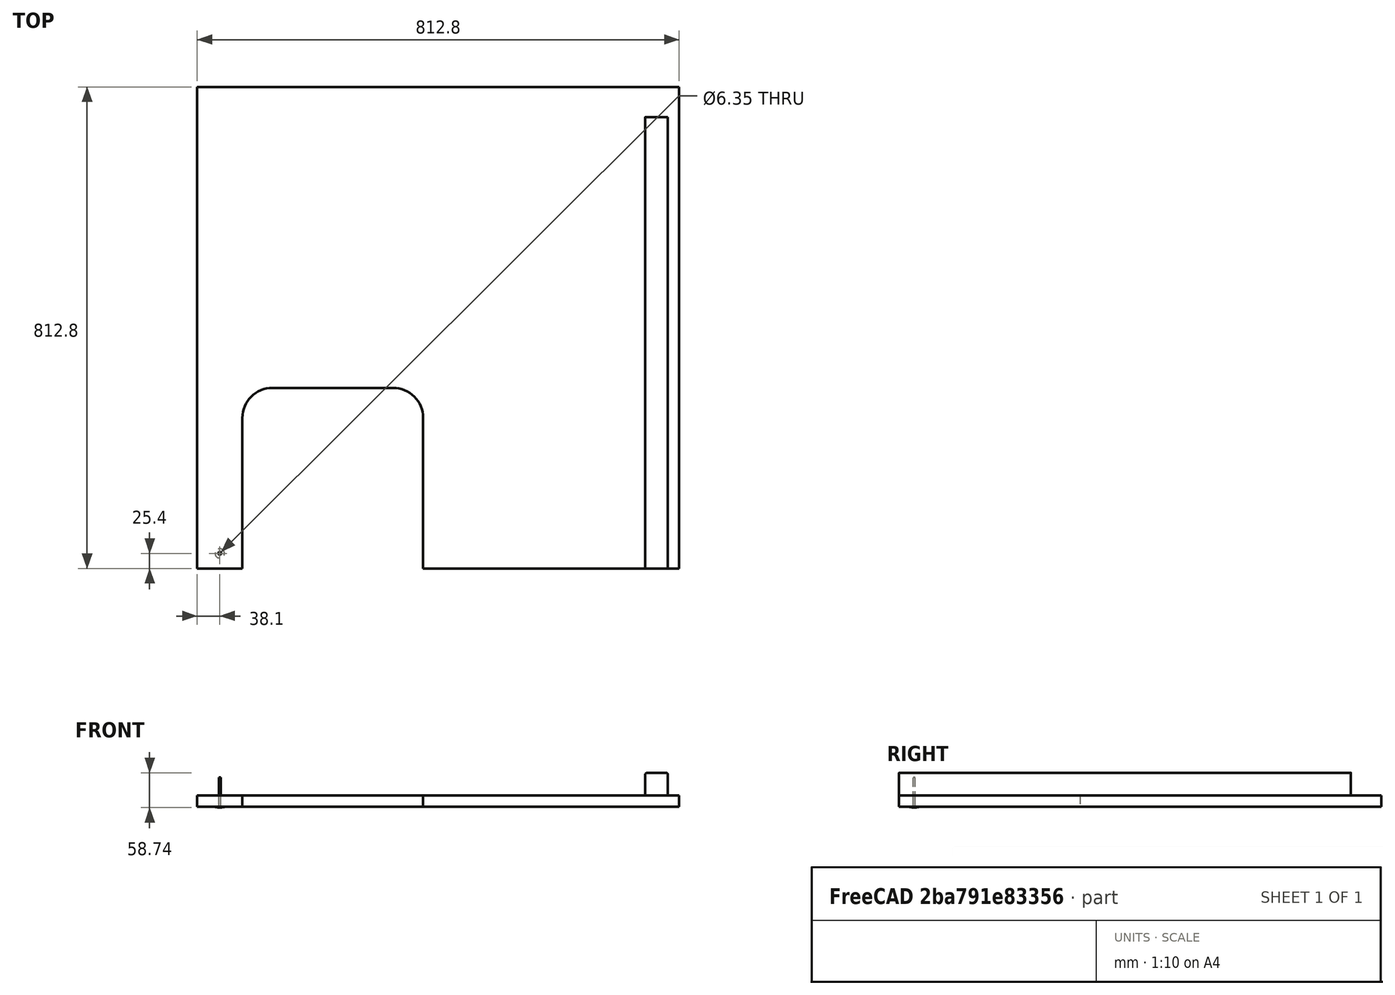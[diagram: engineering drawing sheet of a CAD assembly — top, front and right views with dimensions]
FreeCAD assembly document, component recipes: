
FREECAD ASSEMBLY — COMPONENT RECIPES ("Outlet_Wall")

This assembly document has 7 components, labeled P0..P6 below (a component is one placed body or linked part). 0 of them carry a construction recipe — the FreeCAD feature program that regenerates the part from scratch, quoted from this document or its linked companion documents; the rest are supplied as boundary geometry only. No exploded tour is included for this assembly.
COMPONENT P0 — geometry summary ("IF_A001"; no construction recipe available for this part):
  bounding box: 762.0 x 38.1 x 38.1 mm
  tessellated surface: 332 triangles
  volume: 1099533 mm^3 (99% of its bounding box)
  symmetry: 2-fold rotationally symmetric about the x axis; 4-fold rotationally symmetric about the y axis; 2-fold rotationally symmetric about the z axis; mirror-symmetric across its x mid-plane, y mid-plane, z mid-plane
COMPONENT P1 — geometry summary ("Screw_w_Washer_B001"; no construction recipe available for this part):
  bounding box: 50.8 x 15.9 x 15.9 mm
  tessellated surface: 3,366 triangles
  volume: 650 mm^3 (5% of its bounding box)
  symmetry: 4-fold rotationally symmetric about the z axis; mirror-symmetric across its x mid-plane, y mid-plane
COMPONENT P2 — geometry summary ("Screw_w_Washer_B002"; no construction recipe available for this part):
  bounding box: 50.8 x 15.9 x 15.9 mm
  tessellated surface: 3,366 triangles
  volume: 650 mm^3 (5% of its bounding box)
  symmetry: 4-fold rotationally symmetric about the z axis; mirror-symmetric across its x mid-plane, y mid-plane
COMPONENT P3 — geometry summary ("Screw_w_Washer_B003"; no construction recipe available for this part):
  bounding box: 50.8 x 15.9 x 15.9 mm
  tessellated surface: 3,366 triangles
  volume: 650 mm^3 (5% of its bounding box)
  symmetry: 4-fold rotationally symmetric about the z axis; mirror-symmetric across its x mid-plane, y mid-plane
COMPONENT P4 — geometry summary ("Screw_w_Washer_B004"; no construction recipe available for this part):
  bounding box: 50.8 x 15.9 x 15.9 mm
  tessellated surface: 3,366 triangles
  volume: 650 mm^3 (5% of its bounding box)
  symmetry: 4-fold rotationally symmetric about the z axis; mirror-symmetric across its x mid-plane, y mid-plane
COMPONENT P5 — geometry summary ("Screw_w_Washer_B005"; no construction recipe available for this part):
  bounding box: 50.8 x 15.9 x 15.9 mm
  tessellated surface: 3,366 triangles
  volume: 650 mm^3 (5% of its bounding box)
  symmetry: 4-fold rotationally symmetric about the z axis; mirror-symmetric across its x mid-plane, y mid-plane
COMPONENT P6 — geometry summary ("Frame_Screws_A_LinkGroup001"; no construction recipe available for this part):
  bounding box: 727.1 x 50.8 x 15.9 mm
  tessellated surface: 20,196 triangles
  volume: 3897 mm^3 (1% of its bounding box)
  symmetry: 2-fold rotationally symmetric about the z axis; mirror-symmetric across its x mid-plane, y mid-plane
PROVENANCE & LICENSES
A FreeCAD (.FCStd) document from a public repository crawl; recipes are the document's own serialized feature recipes (and, for linked parts, companion documents' recipes).
License: gpl-3.0.
